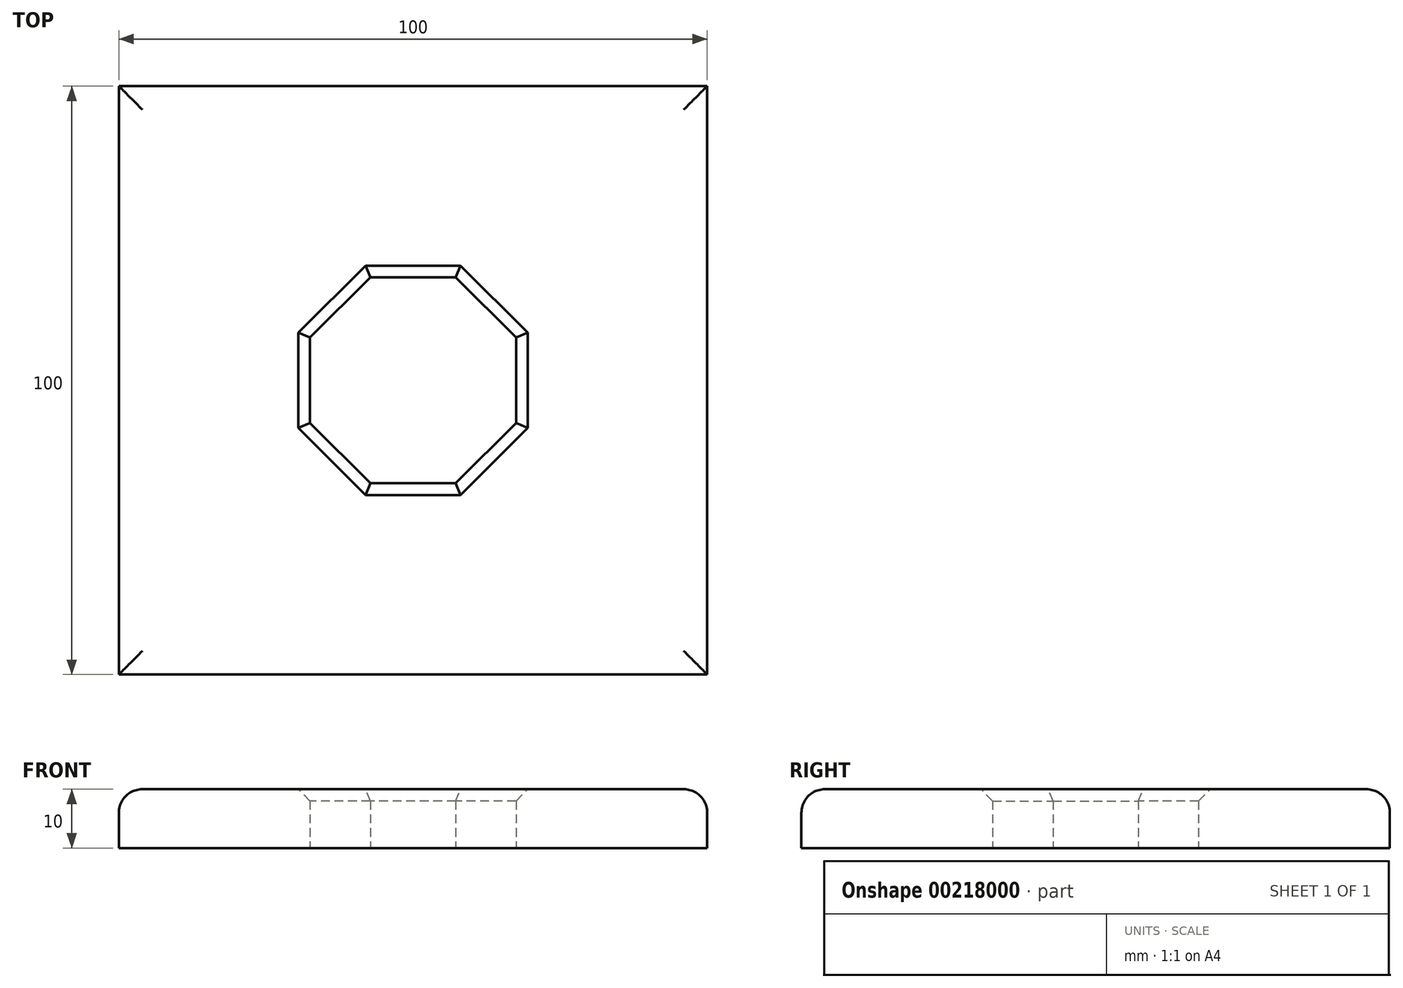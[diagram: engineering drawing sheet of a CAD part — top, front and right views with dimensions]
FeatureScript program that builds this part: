
annotation { "Feature Type Name" : "Feature", "Feature Type Description" : "" }
export const myFeature = defineFeature(function(context is Context, id is Id, definition is map)
    precondition{}
    {
        {
            var Q0;
            Q0=qCreatedBy(makeId("Top.planeOp"),FACE);
            var sketch = newSketch(context, id + "F0", { "sketchPlane" : qUnion([Q0])});
            skLineSegment(sketch, "E0.bottom", {"start": v(-50, 50) * mm, "end": v(50, 50) * mm});
            skLineSegment(sketch, "E0.top", {"start": v(-50, -50) * mm, "end": v(50, -50) * mm});
            skLineSegment(sketch, "E0.left", {"start": v(-50, 50) * mm, "end": v(-50, -50) * mm});
            skLineSegment(sketch, "E0.right", {"start": v(50, 50) * mm, "end": v(50, -50) * mm});
            skPoint(sketch, "E0.middle", {"position": v(0, 0) * mm});
            skCircle(sketch, "E1.cCircle", {"center": v(0, 0) * mm, "radius": 17.5 * mm, "construction": true});
            skLineSegment(sketch, "E1.0", {"start": v(-7.25, 17.5) * mm, "end": v(7.25, 17.5) * mm});
            skLineSegment(sketch, "E1.1", {"start": v(7.25, 17.5) * mm, "end": v(17.5, 7.25) * mm});
            skLineSegment(sketch, "E1.2", {"start": v(17.5, 7.25) * mm, "end": v(17.5, -7.25) * mm});
            skLineSegment(sketch, "E1.3", {"start": v(17.5, -7.25) * mm, "end": v(7.25, -17.5) * mm});
            skLineSegment(sketch, "E1.4", {"start": v(7.25, -17.5) * mm, "end": v(-7.25, -17.5) * mm});
            skLineSegment(sketch, "E1.5", {"start": v(-7.25, -17.5) * mm, "end": v(-17.5, -7.25) * mm});
            skLineSegment(sketch, "E1.6", {"start": v(-17.5, -7.25) * mm, "end": v(-17.5, 7.25) * mm});
            skLineSegment(sketch, "E1.7", {"start": v(-17.5, 7.25) * mm, "end": v(-7.25, 17.5) * mm});
            skPoint(sketch, "E1.0.midPoint", {"position": v(0, 17.5) * mm});
            skSolve(sketch);
        }
        {
            var Q0;
            Q0=makeQuery(id+"F0.imprint","IMPRINT",FACE,{"disambiguationData":[TD([[makeQuery(id+"F0.imprint","IMPRINT",EDGE,{"derivedFrom":sQuery(id+"F0.wireOp",EDGE,"E0.bottom")}),-1.0]])]});
            extrude(context, id + "F1", {"entities" : qUnion([Q0]), "depth" : 10 * mm});
        }
        {
            var Q0;
            Q0=makeQuery(id+"F1.opExtrude","CAP_EDGE",EDGE,{"disambiguationData":[OSD([sQuery(id+"F0.wireOp",EDGE,"E1.0")])],"isStart":false});
            var Q1;
            Q1=makeQuery(id+"F1.opExtrude","CAP_EDGE",EDGE,{"disambiguationData":[OSD([sQuery(id+"F0.wireOp",EDGE,"E1.1")])],"isStart":false});
            var Q2;
            Q2=makeQuery(id+"F1.opExtrude","CAP_EDGE",EDGE,{"disambiguationData":[OSD([sQuery(id+"F0.wireOp",EDGE,"E1.2")])],"isStart":false});
            var Q3;
            Q3=makeQuery(id+"F1.opExtrude","CAP_EDGE",EDGE,{"disambiguationData":[OSD([sQuery(id+"F0.wireOp",EDGE,"E1.3")])],"isStart":false});
            var Q4;
            Q4=makeQuery(id+"F1.opExtrude","CAP_EDGE",EDGE,{"disambiguationData":[OSD([sQuery(id+"F0.wireOp",EDGE,"E1.4")])],"isStart":false});
            var Q5;
            Q5=makeQuery(id+"F1.opExtrude","CAP_EDGE",EDGE,{"disambiguationData":[OSD([sQuery(id+"F0.wireOp",EDGE,"E1.5")])],"isStart":false});
            var Q6;
            Q6=makeQuery(id+"F1.opExtrude","CAP_EDGE",EDGE,{"disambiguationData":[OSD([sQuery(id+"F0.wireOp",EDGE,"E1.6")])],"isStart":false});
            var Q7;
            Q7=makeQuery(id+"F1.opExtrude","CAP_EDGE",EDGE,{"disambiguationData":[OSD([sQuery(id+"F0.wireOp",EDGE,"E1.7")])],"isStart":false});
            chamfer(context, id + "F2", {"entities" : qUnion([Q0, Q1, Q2, Q3, Q4, Q5, Q6, Q7]), "width" : 2 * mm, "tangentPropagation" : true});
        }
        {
            var Q0;
            Q0=makeQuery(id+"F1.opExtrude","CAP_EDGE",EDGE,{"disambiguationData":[OSD([sQuery(id+"F0.wireOp",EDGE,"E0.bottom")])],"isStart":false});
            var Q1;
            Q1=makeQuery(id+"F1.opExtrude","CAP_EDGE",EDGE,{"disambiguationData":[OSD([sQuery(id+"F0.wireOp",EDGE,"E0.right")])],"isStart":false});
            var Q2;
            Q2=makeQuery(id+"F1.opExtrude","CAP_EDGE",EDGE,{"disambiguationData":[OSD([sQuery(id+"F0.wireOp",EDGE,"E0.left")])],"isStart":false});
            var Q3;
            Q3=makeQuery(id+"F1.opExtrude","CAP_EDGE",EDGE,{"disambiguationData":[OSD([sQuery(id+"F0.wireOp",EDGE,"E0.top")])],"isStart":false});
            fillet(context, id + "F3", {"entities" : qUnion([Q0, Q1, Q2, Q3]), "radius" : 4 * mm, "tangentPropagation" : true, "allowEdgeOverflow" : false});
        }
    });
